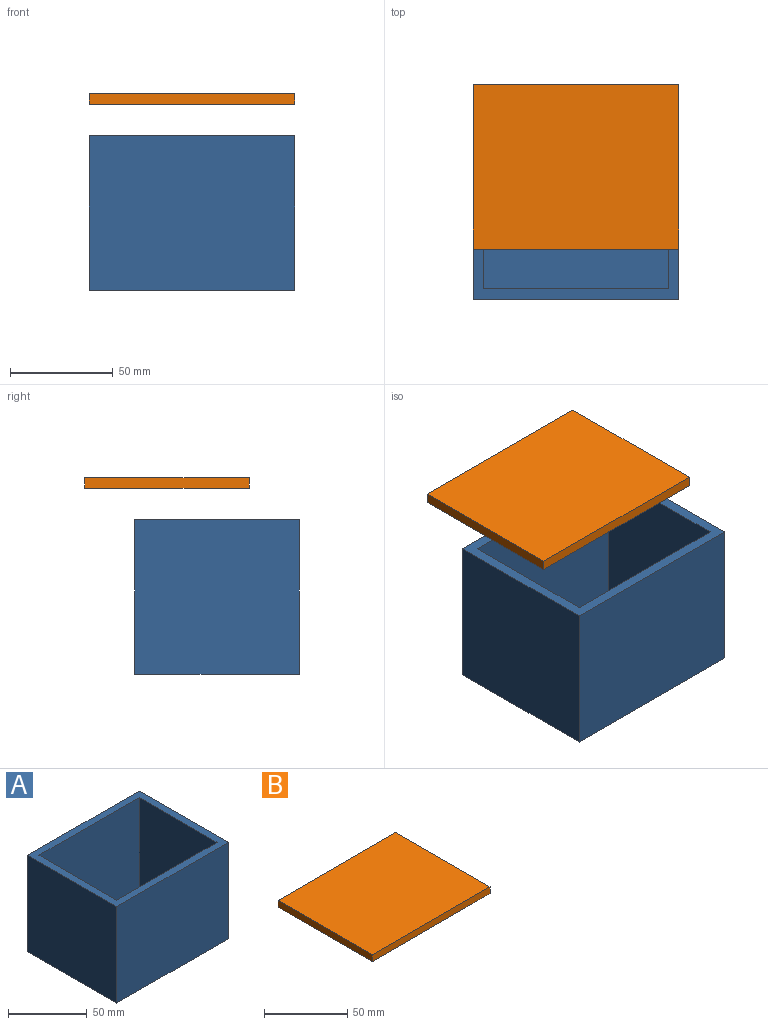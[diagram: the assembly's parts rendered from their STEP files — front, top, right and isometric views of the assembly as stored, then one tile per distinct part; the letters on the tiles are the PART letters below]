
ASSEMBLY  parts=2 mates=1
PART A: 11 faces, bbox 100x80x75 mm
  f0: plane 100x80mm, normal (0,0,1), area 1700mm2, adj f1,f2,f3,f4,f6,f7,f8,f9
  f1: plane 100x75mm, normal (0,1,0), area 7500mm2, adj f0,f2,f4,f5
  f2: plane 80x75mm, normal (-1,0,0), area 6000mm2, adj f0,f1,f3,f5
  f3: plane 100x75mm, normal (0,-1,0), area 7500mm2, adj f0,f2,f4,f5
  f4: plane 80x75mm, normal (1,0,0), area 6000mm2, adj f0,f1,f3,f5
  f5: plane 100x80mm, normal (0,0,-1), area 8000mm2, adj f1,f2,f3,f4
  f6: plane 90x70mm, normal (0,-1,0), area 6300mm2, adj f0,f7,f9,f10
  f7: plane 70x70mm, normal (1,0,0), area 4900mm2, adj f0,f6,f8,f10
  f8: plane 90x70mm, normal (0,1,0), area 6300mm2, adj f0,f7,f9,f10
  f9: plane 70x70mm, normal (-1,0,0), area 4900mm2, adj f0,f6,f8,f10
  f10: plane 90x70mm, normal (0,0,1), area 6300mm2, adj f6,f7,f8,f9
PART B: 6 faces, bbox 100x80x5 mm
  f0: plane 100x5mm, normal (0,1,0), area 500mm2, adj f1,f3,f4,f5
  f1: plane 80x5mm, normal (-1,0,0), area 400mm2, adj f0,f2,f4,f5
  f2: plane 100x5mm, normal (0,-1,0), area 500mm2, adj f1,f3,f4,f5
  f3: plane 80x5mm, normal (1,0,0), area 400mm2, adj f0,f2,f4,f5
  f4: plane 100x80mm, normal (0,0,1), area 8000mm2, adj f0,f1,f2,f3
  f5: plane 100x80mm, normal (0,0,-1), area 8000mm2, adj f0,f1,f2,f3
PLACE A t=(2.41,-15.08,-9.61)mm fixed
PLACE B t=(2.41,9.28,80.82)mm
MATE planar A.f4 <-> B.f3  axis (1,0,0) through (52.41,-15.08,27.89)mm
